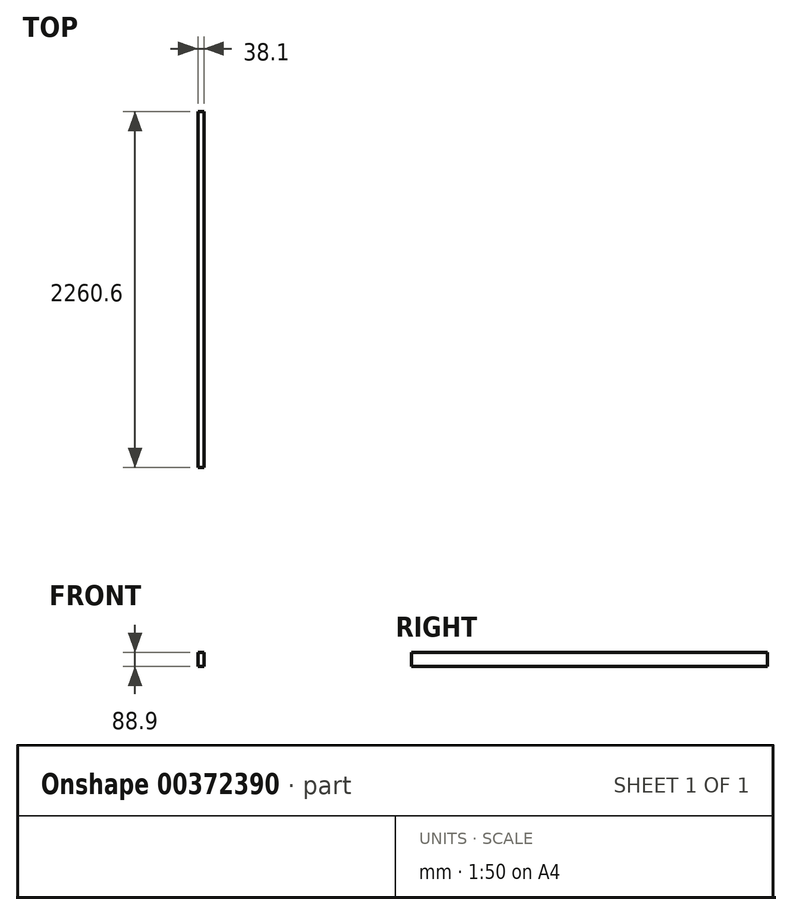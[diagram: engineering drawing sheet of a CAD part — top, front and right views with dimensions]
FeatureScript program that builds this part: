
annotation { "Feature Type Name" : "Feature", "Feature Type Description" : "" }
export const myFeature = defineFeature(function(context is Context, id is Id, definition is map)
    precondition{}
    {
        {
            var Q0;
            Q0=qCreatedBy(makeId("Front.planeOp"),FACE);
            var sketch = newSketch(context, id + "F0", { "sketchPlane" : qUnion([Q0])});
            skLineSegment(sketch, "E0.bottom", {"start": v(-19.05, 44.45) * mm, "end": v(19.05, 44.45) * mm});
            skLineSegment(sketch, "E0.top", {"start": v(-19.05, -44.45) * mm, "end": v(19.05, -44.45) * mm});
            skLineSegment(sketch, "E0.left", {"start": v(-19.05, 44.45) * mm, "end": v(-19.05, -44.45) * mm});
            skLineSegment(sketch, "E0.right", {"start": v(19.05, 44.45) * mm, "end": v(19.05, -44.45) * mm});
            skPoint(sketch, "E0.middle", {"position": v(0, 0) * mm});
            skSolve(sketch);
        }
        {
            var Q0;
            Q0=qSketchRegion(id+"F0",true);
            extrude(context, id + "F1", {"entities" : qUnion([Q0]), "endBound" : BoundingType.SYMMETRIC, "oppositeDirection" : true, "depth" : 2260.6 * mm});
        }
    });
